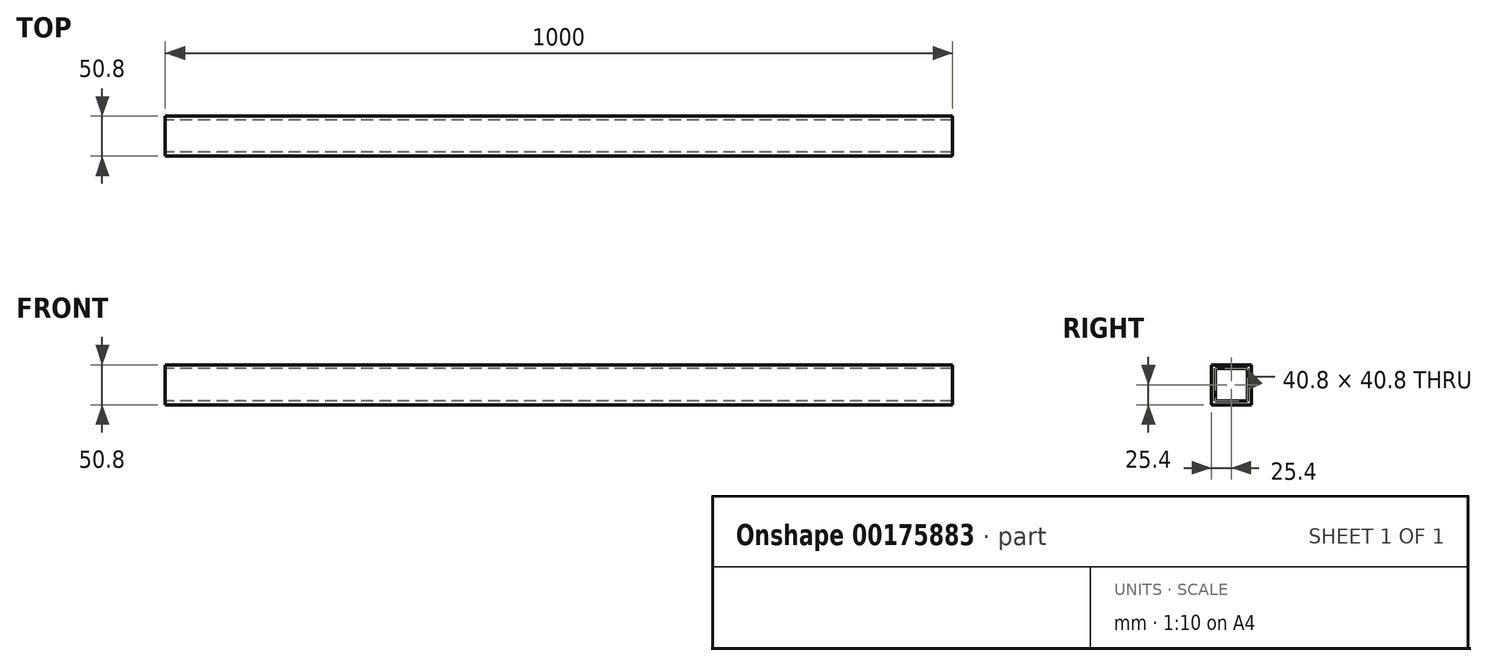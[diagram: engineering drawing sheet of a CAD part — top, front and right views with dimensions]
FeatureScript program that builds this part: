
annotation { "Feature Type Name" : "Feature", "Feature Type Description" : "" }
export const myFeature = defineFeature(function(context is Context, id is Id, definition is map)
    precondition{}
    {
        {
            var Q0;
            Q0=qCreatedBy(makeId("Right.planeOp"),FACE);
            var sketch = newSketch(context, id + "F0", { "sketchPlane" : qUnion([Q0])});
            skLineSegment(sketch, "E0.bottom", {"start": v(-25.4, 25.4) * mm, "end": v(25.4, 25.4) * mm});
            skLineSegment(sketch, "E0.top", {"start": v(-25.4, -25.4) * mm, "end": v(25.4, -25.4) * mm});
            skLineSegment(sketch, "E0.left", {"start": v(-25.4, 25.4) * mm, "end": v(-25.4, -25.4) * mm});
            skLineSegment(sketch, "E0.right", {"start": v(25.4, 25.4) * mm, "end": v(25.4, -25.4) * mm});
            skPoint(sketch, "E0.middle", {"position": v(0, 0) * mm});
            skLineSegment(sketch, "E1.0", {"start": v(-20.4, 20.4) * mm, "end": v(20.4, 20.4) * mm});
            skLineSegment(sketch, "E1.1", {"start": v(-20.4, 20.4) * mm, "end": v(-20.4, -20.4) * mm});
            skLineSegment(sketch, "E1.2", {"start": v(-20.4, -20.4) * mm, "end": v(20.4, -20.4) * mm});
            skLineSegment(sketch, "E1.3", {"start": v(20.4, 20.4) * mm, "end": v(20.4, -20.4) * mm});
            skSolve(sketch);
        }
        {
            var Q0;
            Q0 = qSketchRegion(id + "F0", true);
            extrude(context, id + "F1", {"entities" : qUnion([Q0]), "endBound" : BoundingType.SYMMETRIC, "depth" : 1000 * mm});
        }
    });
